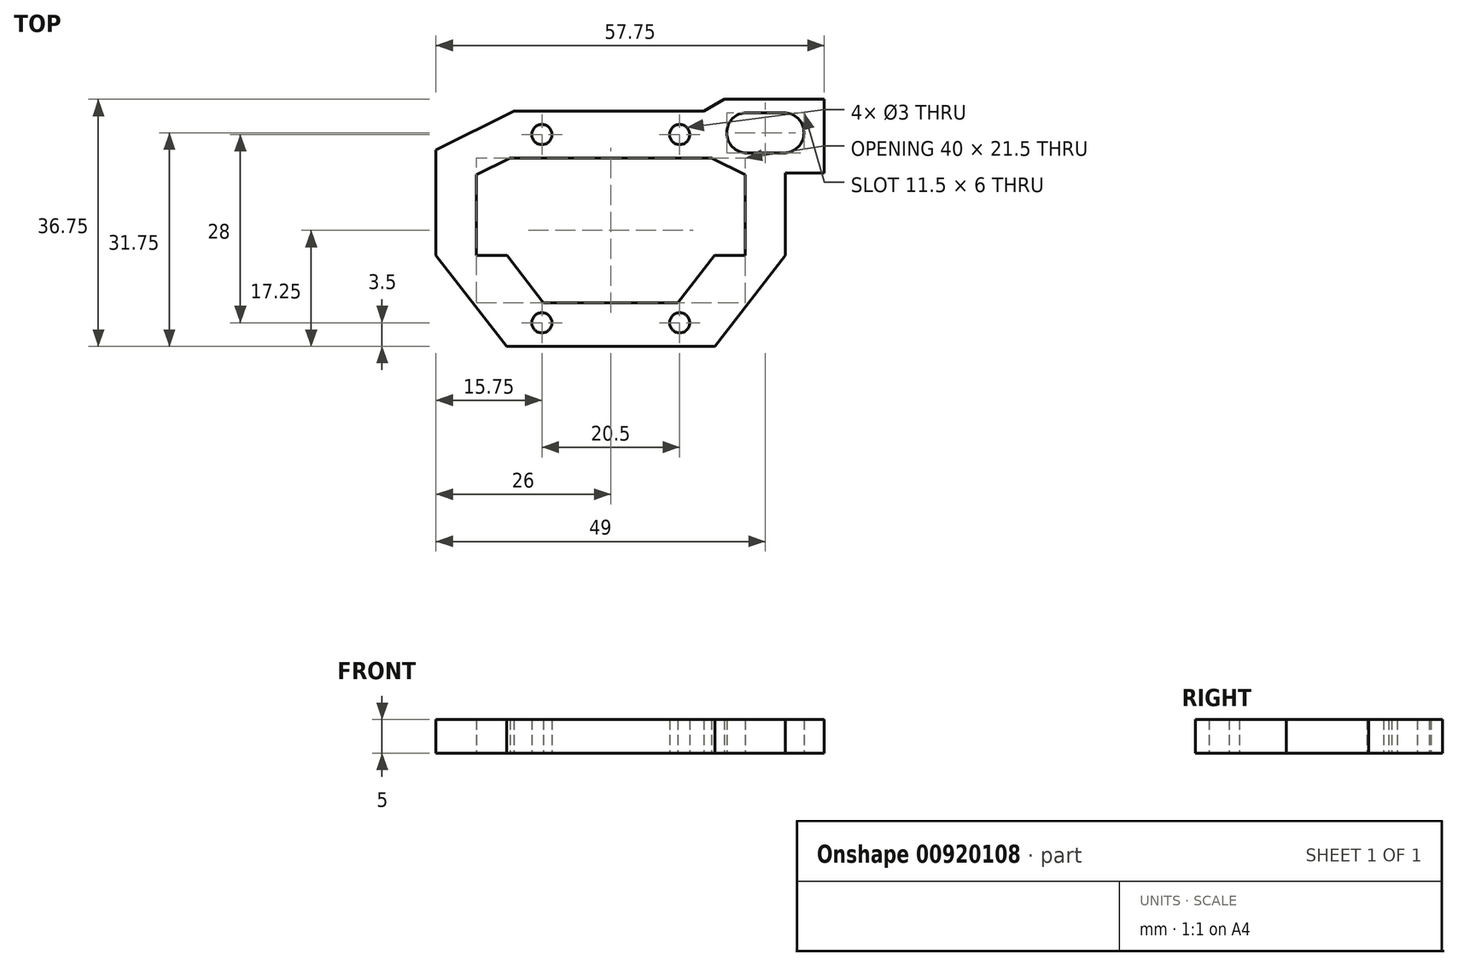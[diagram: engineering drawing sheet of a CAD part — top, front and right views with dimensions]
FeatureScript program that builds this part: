
annotation { "Feature Type Name" : "Feature", "Feature Type Description" : "" }
export const myFeature = defineFeature(function(context is Context, id is Id, definition is map)
    precondition{}
    {
        {
            var Q0;
            Q0=qCreatedBy(makeId("Top.planeOp"),FACE);
            var sketch = newSketch(context, id + "F0", { "sketchPlane" : qUnion([Q0])});
            skLineSegment(sketch, "E0.bottom", {"start": v(10.25, 14) * mm, "end": v(-10.25, 14) * mm, "construction": true});
            skLineSegment(sketch, "E0.top", {"start": v(10.25, -14) * mm, "end": v(-10.25, -14) * mm, "construction": true});
            skLineSegment(sketch, "E0.left", {"start": v(10.25, 14) * mm, "end": v(10.25, -14) * mm, "construction": true});
            skLineSegment(sketch, "E0.right", {"start": v(-10.25, 14) * mm, "end": v(-10.25, -14) * mm, "construction": true});
            skPoint(sketch, "E0.middle", {"position": v(0, 0) * mm});
            skCircle(sketch, "E1", {"center": v(-10.25, 14) * mm, "radius": 1.5 * mm});
            skCircle(sketch, "E2", {"center": v(10.25, 14) * mm, "radius": 1.5 * mm});
            skCircle(sketch, "E3", {"center": v(10.25, -14) * mm, "radius": 1.5 * mm});
            skCircle(sketch, "E4", {"center": v(-10.25, -14) * mm, "radius": 1.5 * mm});
            skArc(sketch, "E5", {"start": v(20.25, 17.25) * mm, "mid": v(17.25, 14.25) * mm, "end": v(20.25, 11.25) * mm});
            skArc(sketch, "E6", {"start": v(25.75, 11.25) * mm, "mid": v(28.75, 14.25) * mm, "end": v(25.75, 17.25) * mm});
            skLineSegment(sketch, "E7", {"start": v(20.25, 17.25) * mm, "end": v(25.75, 17.25) * mm});
            skLineSegment(sketch, "E8", {"start": v(25.75, 11.25) * mm, "end": v(20.25, 11.25) * mm});
            skLineSegment(sketch, "E9", {"start": v(-15.5, -17.5) * mm, "end": v(15.5, -17.5) * mm});
            skLineSegment(sketch, "E10", {"start": v(-20, 8) * mm, "end": v(-20, -4) * mm});
            skLineSegment(sketch, "E11", {"start": v(-20, -4) * mm, "end": v(-15.44, -4) * mm});
            skLineSegment(sketch, "E12", {"start": v(-10, -11) * mm, "end": v(10, -11) * mm});
            skLineSegment(sketch, "E13", {"start": v(15.44, -4) * mm, "end": v(20, -4) * mm});
            skPoint(sketch, "E14", {"position": v(0, -11) * mm});
            skPoint(sketch, "E15", {"position": v(0, -17.5) * mm});
            skLineSegment(sketch, "E16", {"start": v(-15, 10.5) * mm, "end": v(15, 10.5) * mm});
            skLineSegment(sketch, "E17", {"start": v(20, 8) * mm, "end": v(15, 10.5) * mm});
            skLineSegment(sketch, "E18", {"start": v(-20, 8) * mm, "end": v(-15, 10.5) * mm});
            skLineSegment(sketch, "E19.trimOffspring", {"start": v(20, 8) * mm, "end": v(20, -4) * mm});
            skLineSegment(sketch, "E20", {"start": v(-14.42, 17.5) * mm, "end": v(13.88, 17.5) * mm});
            skLineSegment(sketch, "E21", {"start": v(-26, 11.7) * mm, "end": v(-26, -4) * mm});
            skLineSegment(sketch, "E22", {"start": v(-26, -4) * mm, "end": v(-15.5, -17.5) * mm});
            skLineSegment(sketch, "E23", {"start": v(15.5, -17.5) * mm, "end": v(26, -4) * mm});
            skLineSegment(sketch, "E24", {"start": v(26, -4) * mm, "end": v(26, 8.25) * mm});
            skLineSegment(sketch, "E25", {"start": v(26, 8.25) * mm, "end": v(31.75, 8.25) * mm});
            skLineSegment(sketch, "E26", {"start": v(31.75, 8.25) * mm, "end": v(31.75, 19.25) * mm});
            skLineSegment(sketch, "E27", {"start": v(31.75, 19.25) * mm, "end": v(16.91, 19.25) * mm});
            skLineSegment(sketch, "E28", {"start": v(16.91, 19.25) * mm, "end": v(13.88, 17.5) * mm});
            skLineSegment(sketch, "E29", {"start": v(-26, 11.7) * mm, "end": v(-14.42, 17.5) * mm});
            skLineSegment(sketch, "E30", {"start": v(-10, -11) * mm, "end": v(-15.44, -4) * mm});
            skLineSegment(sketch, "E31", {"start": v(10, -11) * mm, "end": v(15.44, -4) * mm});
            skSolve(sketch);
        }
        {
            var Q0;
            Q0=makeQuery(id+"F0.imprint","IMPRINT",FACE,{"disambiguationData":[TD([[makeQuery(id+"F0.imprint","IMPRINT",EDGE,{"derivedFrom":sQuery(id+"F0.wireOp",EDGE,"E1")}),-1.0]])]});
            extrude(context, id + "F1", {"entities" : qUnion([Q0]), "depth" : 5 * mm, "offsetDistance" : 25.4 * mm});
        }
    });
